# Revit family: agtatec_Record_SldngDrset_-ABST-IBST_Generic
name_source: partatom
category: Doors
revit_build: Autodesk Revit Architecture 2015 (Build: 20140606_1530(x64)
units: mm (PartAtom-declared; Revit-internal decimal feet)

## types (12) — shared parameters
A = 1200 mm  [stored 3.93701 ft]
AccessoryOptions = Contact manufacturer
AlternativeDoorsetGlazing = Contact manufacturer
Analytic Construction = <None>
CanopyCovering = agtatec_Record_Revolving Door, Sheet metal (Painted Steel)
CanopyHeight = 220 mm  [stored 0.721785 ft]
CanopyHeightOptions = 200-1000
Category = Curved Sliding Door
Color = Aluminium
Construction Type = Automatic Revolving Door
Description = Curved Sliding Door
Distance = 20 mm  [stored 0.0656168 ft]
DoorIncluded = Yes
DoorsetOperation = automatic
DurationUnit = Year
Finish = Powder coated, Anodized, customer specific
FireExit = No
FloorGuide = Yes
FrameFinishOptions = Stainless steel and more
FrameMaterial = Aluminium
FrameProfile = Aluminium
Function = Exterior
GlassLayers = 2
GlassType = part of glazing spec
HandicapAccessible = No
HasDrive = Yes
Height = 2320 mm  [stored 7.61155 ft]
HeightUnderCanopyOptions = 2200-3000
IfcExportAs = IFCDoorStyle
IfcExportType = Door
IsExternal = Yes
LeafPanelFill = agtatec_Record_Revolving Door, Laminated Safety Glass (Clear)
ManufacturerName = record
ManufacturerURL = www.agta-record.com
Material = Aluminium
ModelReference = depends on the configuration
MountingProfile17mm = Yes
MountingProfile39mm = No
NBSDescription = Sliding Doorset
NBSReference = 25-50-20/175
OpenDoor = No
Operation = automatic
PanelFrames = agtatec_Record_Revolving Door, Aluminium
PassageHeight = 2100 mm
PassageWidth = 1200 mm  [stored 3.93701 ft]
ProductInformation = www.agta-record.com
ReferenceStandard = EN16005, EN16361, DIN 18650, etc.
ReplacementCost = Depends on the configuration and door type
Rough Height = 2320 mm  [stored 7.61155 ft]
Rough Width = 2320 mm  [stored 7.61155 ft]
STRadius = 1200 mm  [stored 3.93701 ft]
SafetyDevices = Optical sensors
SelfClosing = Yes
Size = XxxXXxXX
SmokeStop = No
UnderStructure = No
Uniclass2 = Ss_25_30_20_77
Version = Version 1.0
WarrantyDescription = Depends on country
WarrantyDurationLabour = Depends on country
WarrantyDurationParts = Depends on country
WarrantyDurationUnit = Depends on country
WarrantyGuarantorLabour = Local door manufacturer
WarrantyGuarantorParts = Local door manufacturer
Weight = 0.00 kg
Width = 2320 mm  [stored 7.61155 ft]
WithinStandardSizes = Yes
zero-valued in all types: Cost, GlassThickness1, GlassThickness2, GlassThickness3, GlazingAreaFraction, NominalHeight, NominalLength, NominalWidth, ThermalTransmittance, Thickness

## per-type parameters (varying)
- ABST With Side Panels - 20 mm: ABST=Yes; ABSTWith20=Yes; ABSTWith30=No; ABSTWithout20=No; ABSTWithout30=No; BIMObjectName=agtatec_Record_SldngDrset_ABST Circular-slidingDoor_WallBased; CanopyRoof=Yes; CanopyRoofRadius=1164 mm; Features=Air curtain; FloorChannel=No; H=727.29 mm; IBST=No; IBSTWith20=No; IBSTWith30=No; IBSTWithout20=No; IBSTWithout30=No; Name=SldngDrset_ABST Circular-slidingDoor_Generic_Record; Panel20mm=Yes; Panel30mm=No; PassageWidthOptions=contact manufacturer; RST180=No; RST18020=No; RST18030=No; RST360=No; RST36020=No; RST36030=No; STRadiusABSTCanopy=1180 mm  [stored 3.87139 ft]; STWidth=20 mm  [stored 0.0656168 ft]; SW=35.04°; SWAdd=3.29°; Shape=Half-Cylinder Shaped; TFDichtung=20 mm  [stored 0.0656168 ft]; TFWidth=20 mm  [stored 0.0656168 ft]; URL=www.agta-record.com
www.agta-record.com
www.agta-record.com
www.agta-record.com
www.agta-record.com
www.agta-record.com; W=31.76°; WL=458.53 mm; WithSidePanels=Yes; WithoutSidePanels=No
- ABST With Side Panels - 30 mm: ABST=Yes; ABSTWith20=No; ABSTWith30=Yes; ABSTWithout20=No; ABSTWithout30=No; BIMObjectName=agtatec_Record_SldngDrset_ABST Circular-slidingDoor_WallBased; CanopyRoof=Yes; CanopyRoofRadius=1164 mm; Features=Air curtain; FloorChannel=No; H=761.01 mm; IBST=No; IBSTWith20=No; IBSTWith30=No; IBSTWithout20=No; IBSTWithout30=No; Name=SldngDrset_ABST Circular-slidingDoor_Generic_Record; Panel20mm=No; Panel30mm=Yes; PassageWidthOptions=contact manufacturer; RST180=No; RST18020=No; RST18030=No; RST360=No; RST36020=No; RST36030=No; STRadiusABSTCanopy=1170 mm; STWidth=30 mm  [stored 0.0984252 ft]; SW=36.15°; SWAdd=3.76°; Shape=Half-Cylinder Shaped; TFDichtung=30 mm  [stored 0.0984252 ft]; TFWidth=30 mm  [stored 0.0984252 ft]; URL=www.agta-record.com; W=32.39°; WL=425.82 mm; WithSidePanels=Yes; WithoutSidePanels=No
- ABST Without Side Panels - 20 mm: ABST=Yes; ABSTWith20=No; ABSTWith30=No; ABSTWithout20=Yes; ABSTWithout30=No; BIMObjectName=agtatec_Record_SldngDrset_ABST Circular-slidingDoor_WallBased; CanopyRoof=Yes; CanopyRoofRadius=1200 mm  [stored 3.93701 ft]; Features=Air curtain; FloorChannel=No; H=727.29 mm; IBST=No; IBSTWith20=No; IBSTWith30=No; IBSTWithout20=No; IBSTWithout30=No; Name=SldngDrset_ABST Circular-slidingDoor_Generic_Record; Panel20mm=Yes; Panel30mm=No; PassageWidthOptions=contact manufacturer; RST180=No; RST18020=No; RST18030=No; RST360=No; RST36020=No; RST36030=No; STRadiusABSTCanopy=1180 mm  [stored 3.87139 ft]; STWidth=20 mm  [stored 0.0656168 ft]; SW=35.04°; SWAdd=3.29°; Shape=Half-Cylinder Shaped; TFDichtung=20 mm  [stored 0.0656168 ft]; TFWidth=20 mm  [stored 0.0656168 ft]; URL=www.agta-record.com; W=31.76°; WL=472.71 mm; WithSidePanels=No; WithoutSidePanels=Yes
- ABST Without Side Panels - 30 mm: ABST=Yes; ABSTWith20=No; ABSTWith30=No; ABSTWithout20=No; ABSTWithout30=Yes; BIMObjectName=agtatec_Record_SldngDrset_ABST Circular-slidingDoor_WallBased; CanopyRoof=Yes; CanopyRoofRadius=1200 mm  [stored 3.93701 ft]; Features=Air curtain; FloorChannel=Yes; H=761.01 mm; IBST=No; IBSTWith20=No; IBSTWith30=No; IBSTWithout20=No; IBSTWithout30=No; Name=SldngDrset_ABST Circular-slidingDoor_Generic_Record; Panel20mm=No; Panel30mm=Yes; PassageWidthOptions=contact manufacturer; RST180=No; RST18020=No; RST18030=No; RST360=No; RST36020=No; RST36030=No; STRadiusABSTCanopy=1170 mm; STWidth=30 mm  [stored 0.0984252 ft]; SW=36.15°; SWAdd=3.76°; Shape=Half-Cylinder Shaped; TFDichtung=30 mm  [stored 0.0984252 ft]; TFWidth=30 mm  [stored 0.0984252 ft]; URL=www.agta-record.com; W=32.39°; WL=438.99 mm; WithSidePanels=No; WithoutSidePanels=Yes
- IBST With Side Panels - 20 mm: ABST=No; ABSTWith20=No; ABSTWith30=No; ABSTWithout20=No; ABSTWithout30=No; BIMObjectName=agtatec_Record_SldngDrset_IBST-circular-slidingDoor_WallBased; CanopyRoof=Yes; CanopyRoofRadius=900 mm  [stored 2.95276 ft]; Features=Air curtain; FloorChannel=No; H=731.74 mm; IBST=Yes; IBSTWith20=Yes; IBSTWith30=No; IBSTWithout20=No; IBSTWithout30=No; Name=SldngDrset_IBST-circular-slidingDoor_Generic_Record; Panel20mm=Yes; Panel30mm=No; PassageWidthOptions=contact manufacturer; RST180=No; RST18020=No; RST18030=No; RST360=No; RST36020=No; RST36030=No; STRadiusABSTCanopy=1180 mm  [stored 3.87139 ft]; STWidth=20 mm  [stored 0.0656168 ft]; SW=35.28°; SWAdd=3.52°; Shape=Half-Cylinder Shaped; TFDichtung=20 mm  [stored 0.0656168 ft]; TFWidth=20 mm  [stored 0.0656168 ft]; URL=www.agta-record.com; W=31.76°; WL=351.2 mm; WithSidePanels=Yes; WithoutSidePanels=No
- IBST With Side Panels - 30 mm: ABST=No; ABSTWith20=No; ABSTWith30=No; ABSTWithout20=No; ABSTWithout30=No; BIMObjectName=agtatec_Record_SldngDrset_IBST-circular-slidingDoor_WallBased; CanopyRoof=Yes; CanopyRoofRadius=900 mm  [stored 2.95276 ft]; Features=Air curtain; FloorChannel=No; H=767.56 mm; IBST=Yes; IBSTWith20=No; IBSTWith30=Yes; IBSTWithout20=No; IBSTWithout30=No; Name=SldngDrset_IBST-circular-slidingDoor_Generic_Record; Panel20mm=No; Panel30mm=Yes; PassageWidthOptions=contact manufacturer; RST180=No; RST18020=No; RST18030=No; RST360=No; RST36020=No; RST36030=No; STRadiusABSTCanopy=1170 mm; STWidth=30 mm  [stored 0.0984252 ft]; SW=36.48°; SWAdd=4.09°; Shape=Half-Cylinder Shaped; TFDichtung=30 mm  [stored 0.0984252 ft]; TFWidth=30 mm  [stored 0.0984252 ft]; URL=www.agta-record.com; W=32.39°; WL=324.33 mm; WithSidePanels=Yes; WithoutSidePanels=No
- IBST Without Side Panels - 20 mm: ABST=No; ABSTWith20=No; ABSTWith30=No; ABSTWithout20=No; ABSTWithout30=No; BIMObjectName=agtatec_Record_SldngDrset_IBST-circular-slidingDoor_WallBased; CanopyRoof=Yes; CanopyRoofRadius=902.8 mm; Features=Air curtain; FloorChannel=No; H=731.74 mm; IBST=Yes; IBSTWith20=No; IBSTWith30=No; IBSTWithout20=Yes; IBSTWithout30=No; Name=SldngDrset_IBST-circular-slidingDoor_Generic_Record; Panel20mm=Yes; Panel30mm=No; PassageWidthOptions=contact manufacturer; RST180=No; RST18020=No; RST18030=No; RST360=No; RST36020=No; RST36030=No; STRadiusABSTCanopy=1180 mm  [stored 3.87139 ft]; STWidth=20 mm  [stored 0.0656168 ft]; SW=35.28°; SWAdd=3.52°; Shape=Half-Cylinder Shaped; TFDichtung=20 mm  [stored 0.0656168 ft]; TFWidth=20 mm  [stored 0.0656168 ft]; URL=www.agta-record.com; W=31.76°; WL=352.29 mm; WithSidePanels=No; WithoutSidePanels=Yes
- IBST Without Side Panels - 30 mm: ABST=No; ABSTWith20=No; ABSTWith30=No; ABSTWithout20=No; ABSTWithout30=No; BIMObjectName=agtatec_Record_SldngDrset_IBST-circular-slidingDoor_WallBased; CanopyRoof=Yes; CanopyRoofRadius=903 mm  [stored 2.9626 ft]; Features=Air curtain; FloorChannel=No; H=767.56 mm; IBST=Yes; IBSTWith20=No; IBSTWith30=No; IBSTWithout20=No; IBSTWithout30=Yes; Name=SldngDrset_IBST-circular-slidingDoor_Generic_Record; Panel20mm=No; Panel30mm=Yes; PassageWidthOptions=contact manufacturer; RST180=No; RST18020=No; RST18030=No; RST360=No; RST36020=No; RST36030=No; STRadiusABSTCanopy=1170 mm; STWidth=30 mm  [stored 0.0984252 ft]; SW=36.48°; SWAdd=4.09°; Shape=Half-Cylinder Shaped; TFDichtung=30 mm  [stored 0.0984252 ft]; TFWidth=30 mm  [stored 0.0984252 ft]; URL=www.agta-record.com; W=32.39°; WL=325.41 mm; WithSidePanels=No; WithoutSidePanels=Yes
- RST 180 - 20 mm: ABST=No; ABSTWith20=No; ABSTWith30=No; ABSTWithout20=No; ABSTWithout30=No; BIMObjectName=agtatec_Record_SldngDrset_RST-circular-slidingDoo_WallBased; CanopyRoof=No; CanopyRoofRadius=1200 mm  [stored 3.93701 ft]; DiameterOptions=1500-3600; Features=Air curtain; FloorChannel=No; H=1200 mm  [stored 3.93701 ft]; IBST=No; IBSTWith20=No; IBSTWith30=No; IBSTWithout20=No; IBSTWithout30=No; Name=SldngDrset_RST-circular-slidingDoor_Generic_Record; Panel20mm=Yes; Panel30mm=No; PassageWidthOptions=1005-2451; RST180=Yes; RST18020=Yes; RST18030=No; RST360=No; RST36020=No; RST36030=No; STRadiusABSTCanopy=1180 mm  [stored 3.87139 ft]; STWidth=20 mm  [stored 0.0656168 ft]; SW=58.24°; SWAdd=3.29°; Shape=Half-Cylinder Shaped; TFDichtung=20 mm  [stored 0.0656168 ft]; TFWidth=20 mm  [stored 0.0656168 ft]; URL=www.agta-record.com; W=31.76°; WL=0 mm  [stored 0 ft]; WithSidePanels=Yes; WithoutSidePanels=No
- RST 180 - 30 mm: ABST=No; ABSTWith20=No; ABSTWith30=No; ABSTWithout20=No; ABSTWithout30=No; BIMObjectName=agtatec_Record_SldngDrset_RST-circular-slidingDoo_WallBased; CanopyRoof=No; CanopyRoofRadius=1200 mm  [stored 3.93701 ft]; DiameterOptions=1500-3600; Features=Air curtain; FloorChannel=No; H=1200 mm  [stored 3.93701 ft]; IBST=No; IBSTWith20=No; IBSTWith30=No; IBSTWithout20=No; IBSTWithout30=No; Name=SldngDrset_RST-circular-slidingDoor_Generic_Record; Panel20mm=No; Panel30mm=Yes; PassageWidthOptions=1005-2451; RST180=Yes; RST18020=No; RST18030=Yes; RST360=No; RST36020=No; RST36030=No; STRadiusABSTCanopy=1170 mm; STWidth=30 mm  [stored 0.0984252 ft]; SW=57.61°; SWAdd=3.76°; Shape=Half-Cylinder Shaped; TFDichtung=30 mm  [stored 0.0984252 ft]; TFWidth=30 mm  [stored 0.0984252 ft]; URL=www.agta-record.com; W=32.39°; WL=0 mm  [stored 0 ft]; WithSidePanels=Yes; WithoutSidePanels=No
- RST 360 - 20 mm: ABST=No; ABSTWith20=No; ABSTWith30=No; ABSTWithout20=No; ABSTWithout30=No; BIMObjectName=agtatec_Record_SldngDrset_RTS-circular-slidingDoo_WallBased; CanopyRoof=No; CanopyRoofRadius=1200 mm  [stored 3.93701 ft]; DiameterOptions=1500-3600; Features=Sluice function, air curtain; FloorChannel=No; H=1200 mm  [stored 3.93701 ft]; IBST=No; IBSTWith20=No; IBSTWith30=No; IBSTWithout20=No; IBSTWithout30=No; Name=SldngDrset_RST-circular-slidingDoor_Generic_Record; Panel20mm=Yes; Panel30mm=No; PassageWidthOptions=1005-2451; RST180=No; RST18020=No; RST18030=No; RST360=Yes; RST36020=Yes; RST36030=No; STRadiusABSTCanopy=1180 mm  [stored 3.87139 ft]; STWidth=20 mm  [stored 0.0656168 ft]; SW=58.24°; SWAdd=3.29°; Shape=Full Cylinder Shaped; TFDichtung=20 mm  [stored 0.0656168 ft]; TFWidth=20 mm  [stored 0.0656168 ft]; URL=www.agta-record.com; W=31.76°; WL=0 mm  [stored 0 ft]; WithSidePanels=Yes; WithoutSidePanels=No
- RST 360 - 30 mm: ABST=No; ABSTWith20=No; ABSTWith30=No; ABSTWithout20=No; ABSTWithout30=No; BIMObjectName=agtatec_Record_SldngDrset_RTS-circular-slidingDoo_WallBased; CanopyRoof=No; CanopyRoofRadius=1200 mm  [stored 3.93701 ft]; DiameterOptions=1500-3600; Features=Sluice function, air curtain; FloorChannel=No; H=1200 mm  [stored 3.93701 ft]; IBST=No; IBSTWith20=No; IBSTWith30=No; IBSTWithout20=No; IBSTWithout30=No; Name=SldngDrset_RST-circular-slidingDoor_Generic_Record; Panel20mm=No; Panel30mm=Yes; PassageWidthOptions=1005-2451; RST180=No; RST18020=No; RST18030=No; RST360=Yes; RST36020=No; RST36030=Yes; STRadiusABSTCanopy=1170 mm; STWidth=30 mm  [stored 0.0984252 ft]; SW=57.61°; SWAdd=3.76°; Shape=Full Cylinder Shaped; TFDichtung=30 mm  [stored 0.0984252 ft]; TFWidth=30 mm  [stored 0.0984252 ft]; URL=www.agta-record.com; W=32.39°; WL=0 mm  [stored 0 ft]; WithSidePanels=Yes; WithoutSidePanels=No

note: [stored X ft] marks values corroborated as IEEE doubles in the binary element streams (Revit-internal decimal feet)

## geometry (parser evidence)
native form markers: Sweep x2
no freeform markers — native parametric forms only
